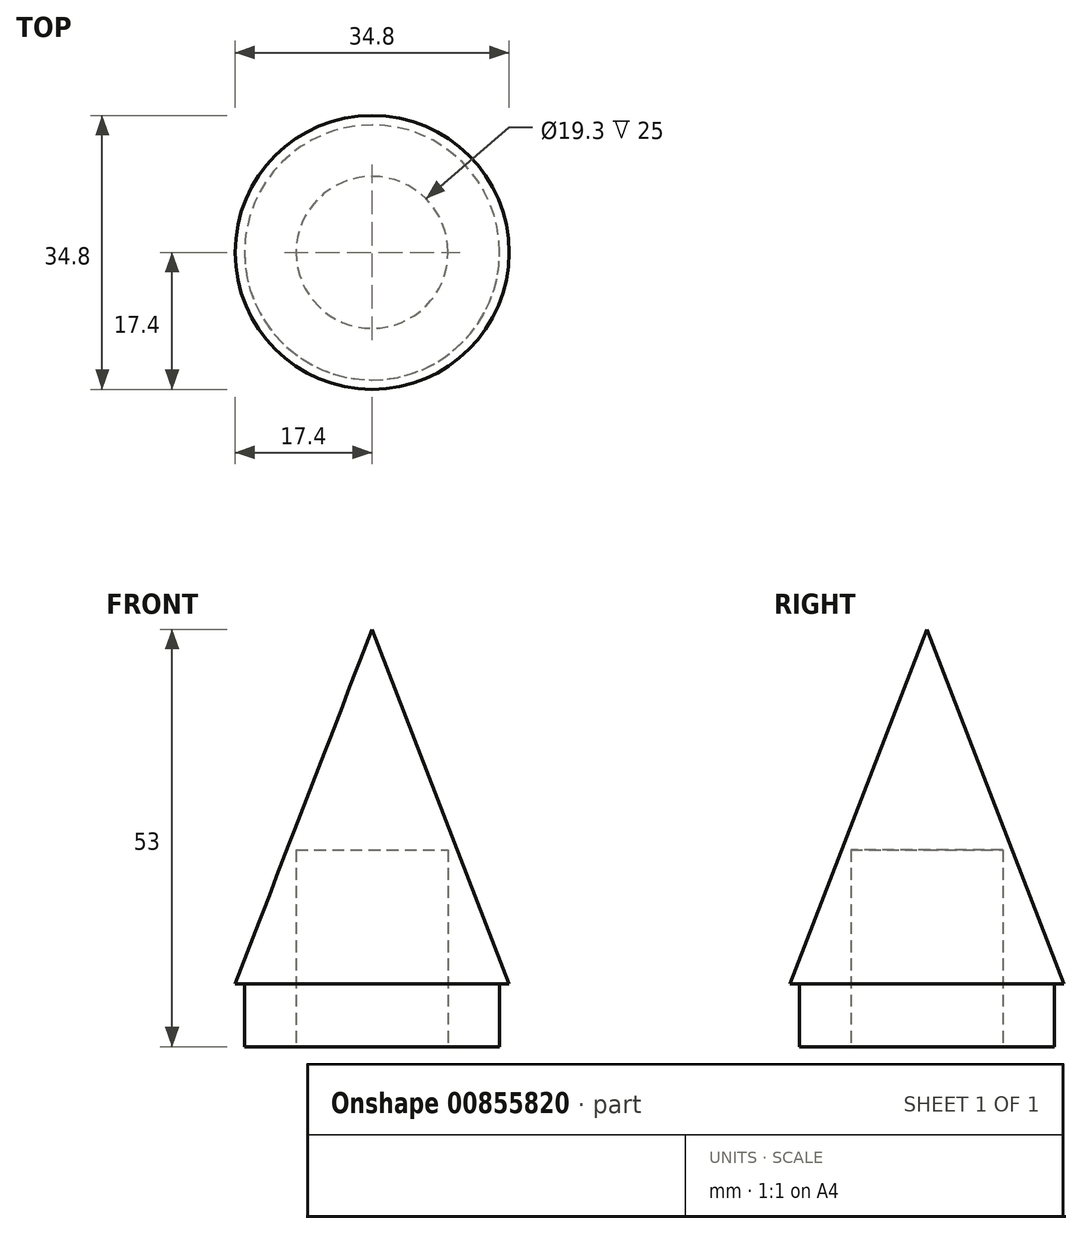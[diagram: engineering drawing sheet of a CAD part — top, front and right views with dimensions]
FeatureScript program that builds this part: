
annotation { "Feature Type Name" : "Feature", "Feature Type Description" : "" }
export const myFeature = defineFeature(function(context is Context, id is Id, definition is map)
    precondition{}
    {
        {
            var Q0;
            Q0=qCreatedBy(makeId("Front.planeOp"),FACE);
            var sketch = newSketch(context, id + "F0", { "sketchPlane" : qUnion([Q0])});
            skLineSegment(sketch, "E0", {"start": v(0, 0) * mm, "end": v(-17.4, 0) * mm});
            skLineSegment(sketch, "E1", {"start": v(-17.4, 0) * mm, "end": v(0, 45) * mm});
            skLineSegment(sketch, "E2", {"start": v(0, 45) * mm, "end": v(0, 0) * mm});
            skSolve(sketch);
        }
        {
            var Q0;
            Q0=makeQuery(id+"F0.imprint","IMPRINT",FACE,{"disambiguationData":[TD([[makeQuery(id+"F0.imprint","IMPRINT",EDGE,{"derivedFrom":sQuery(id+"F0.wireOp",EDGE,"E0")}),-1.0]])]});
            var Q1;
            Q1=sQuery(id+"F0.wireOp",EDGE,"E2");
            revolve(context, id + "F1", {"surfaceOperationType" : NewSurfaceOperationType.NEW, "entities" : qUnion([Q0]), "axis" : qUnion([Q1]), "revolveType" : RevolveType.FULL});
        }
        {
            var Q0;
            Q0=makeQuery(id+"F1.opRevolve","SWEPT_FACE",FACE,{"disambiguationData":[OSD([sQuery(id+"F0.wireOp",EDGE,"E0")])]});
            var sketch = newSketch(context, id + "F2", { "sketchPlane" : qUnion([Q0])});
            skCircle(sketch, "E3", {"center": v(0, 0) * mm, "radius": 16.2 * mm});
            skSolve(sketch);
        }
        {
            var Q0;
            Q0 = qSketchRegion(id + "F2", true);
            extrude(context, id + "F3", {"entities" : qUnion([Q0]), "operationType" : NewBodyOperationType.ADD, "depth" : 8 * mm, "offsetDistance" : 25 * mm});
        }
        {
            var Q0;
            Q0=makeQuery(id+"F3.opExtrude","CAP_FACE",FACE,{"disambiguationData":[OSD([sQuery(id+"F2.wireOp",EDGE,"E3")])],"isStart":false});
            var sketch = newSketch(context, id + "F4", { "sketchPlane" : qUnion([Q0])});
            skCircle(sketch, "E4", {"center": v(0, 0) * mm, "radius": 9.65 * mm});
            skSolve(sketch);
        }
        {
            var Q0;
            Q0=makeQuery(id+"F4.imprint","IMPRINT",FACE,{"disambiguationData":[TD([[makeQuery(id+"F4.imprint","IMPRINT",EDGE,{"derivedFrom":sQuery(id+"F4.wireOp",EDGE,"E4")}),1.0]])]});
            extrude(context, id + "F5", {"entities" : qUnion([Q0]), "operationType" : NewBodyOperationType.REMOVE, "oppositeDirection" : true, "depth" : 25 * mm, "offsetDistance" : 25 * mm});
        }
    });
